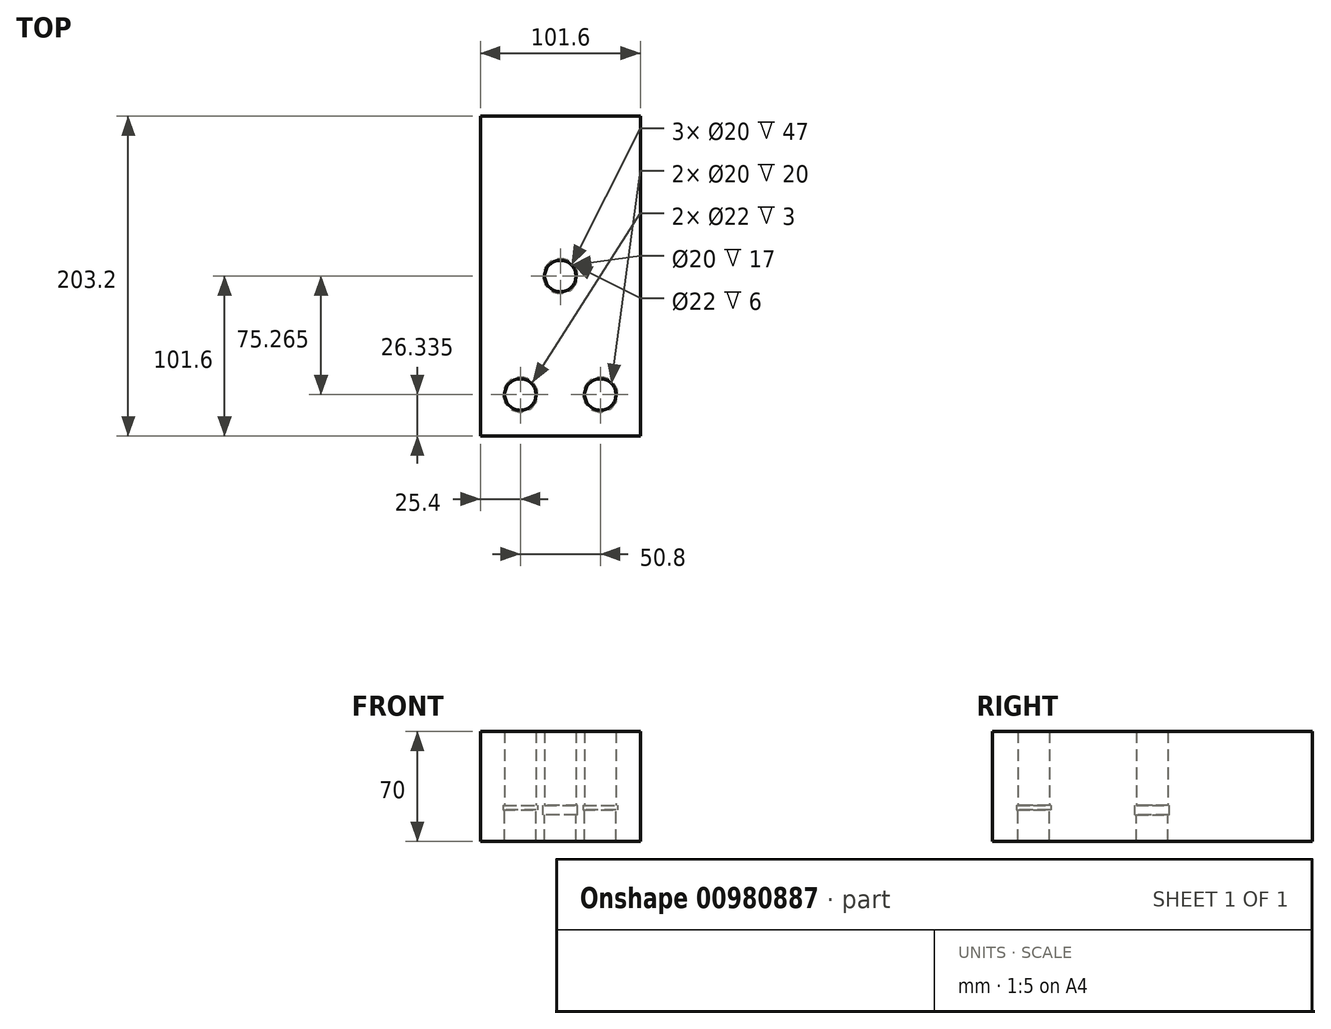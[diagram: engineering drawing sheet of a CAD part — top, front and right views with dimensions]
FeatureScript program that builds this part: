
annotation { "Feature Type Name" : "Feature", "Feature Type Description" : "" }
export const myFeature = defineFeature(function(context is Context, id is Id, definition is map)
    precondition{}
    {
        {
            var Q0;
            Q0=qCreatedBy(makeId("Top.planeOp"),FACE);
            var sketch = newSketch(context, id + "F0", { "sketchPlane" : qUnion([Q0])});
            skLineSegment(sketch, "E0.bottom", {"start": v(-50.8, -101.6) * mm, "end": v(50.8, -101.6) * mm});
            skLineSegment(sketch, "E0.top", {"start": v(-50.8, 101.6) * mm, "end": v(50.8, 101.6) * mm});
            skLineSegment(sketch, "E0.left", {"start": v(-50.8, -101.6) * mm, "end": v(-50.8, 101.6) * mm});
            skLineSegment(sketch, "E0.right", {"start": v(50.8, -101.6) * mm, "end": v(50.8, 101.6) * mm});
            skPoint(sketch, "E0.middle", {"position": v(0, 0) * mm});
            skPoint(sketch, "E1", {"position": v(-25.4, -75.26) * mm});
            skPoint(sketch, "E2", {"position": v(25.4, -75.26) * mm});
            skSolve(sketch);
        }
        {
            var Q0;
            Q0 = qSketchRegion(id + "F0", true);
            extrude(context, id + "F1", {"entities" : qUnion([Q0]), "oppositeDirection" : true, "depth" : 20 * mm, "offsetDistance" : 25.4 * mm});
        }
        {
            var Q0;
            Q0=sQuery(id+"F0.wireOp",VERTEX,"E0.middle");
            var Q1;
            Q1=makeQuery(id+"F1.opExtrude","SWEPT_BODY",BODY,{"disambiguationData":[OSD([sQuery(id+"F0.wireOp",EDGE,"E0.bottom"),sQuery(id+"F0.wireOp",EDGE,"E0.top"),sQuery(id+"F0.wireOp",EDGE,"E0.left"),sQuery(id+"F0.wireOp",EDGE,"E0.right")])]});
            hole(context, id + "F2", {"style" : HoleStyle.C_BORE, "endStyle" : HoleEndStyle.THROUGH, "holeDiameter" : 20 * mm, "cBoreDiameter" : 22 * mm, "cBoreDepth" : 3 * mm, "majorDiameter" : 6.35 * mm, "isTappedThrough" : true, "tappedDepth" : 12.7 * mm, "tapClearance" : 3, "startFromSketch" : true, "locations" : qUnion([Q0]), "scope" : qUnion([Q1])});
        }
        {
            var Q0;
            Q0=sQuery(id+"F0.wireOp",VERTEX,"E1");
            var Q1;
            Q1=makeQuery(id+"F1.opExtrude","SWEPT_BODY",BODY,{"disambiguationData":[OSD([sQuery(id+"F0.wireOp",EDGE,"E0.bottom"),sQuery(id+"F0.wireOp",EDGE,"E0.top"),sQuery(id+"F0.wireOp",EDGE,"E0.left"),sQuery(id+"F0.wireOp",EDGE,"E0.right")])]});
            hole(context, id + "F3", {"style" : HoleStyle.SIMPLE, "endStyle" : HoleEndStyle.THROUGH, "holeDiameter" : 20 * mm, "majorDiameter" : 6.35 * mm, "isTappedThrough" : true, "tappedDepth" : 12.7 * mm, "tapClearance" : 3, "startFromSketch" : true, "locations" : qUnion([Q0]), "scope" : qUnion([Q1])});
        }
        {
            var Q0;
            Q0=sQuery(id+"F0.wireOp",VERTEX,"E2");
            var Q1;
            Q1=makeQuery(id+"F1.opExtrude","SWEPT_BODY",BODY,{"disambiguationData":[OSD([sQuery(id+"F0.wireOp",EDGE,"E0.bottom"),sQuery(id+"F0.wireOp",EDGE,"E0.top"),sQuery(id+"F0.wireOp",EDGE,"E0.left"),sQuery(id+"F0.wireOp",EDGE,"E0.right")])]});
            hole(context, id + "F4", {"style" : HoleStyle.SIMPLE, "endStyle" : HoleEndStyle.THROUGH, "holeDiameter" : 20 * mm, "majorDiameter" : 6.35 * mm, "isTappedThrough" : true, "tappedDepth" : 12.7 * mm, "tapClearance" : 3, "startFromSketch" : true, "locations" : qUnion([Q0]), "scope" : qUnion([Q1])});
        }
        {
            var Q0;
            Q0=makeQuery(id+"F0.imprint","IMPRINT",FACE,{"disambiguationData":[TD([[makeQuery(id+"F0.imprint","IMPRINT",EDGE,{"derivedFrom":sQuery(id+"F0.wireOp",EDGE,"E0.bottom")}),1.0]])]});
            var sketch = newSketch(context, id + "F5", { "sketchPlane" : qUnion([Q0])});
            skCircle(sketch, "E3", {"center": v(0, 76.88) * mm, "radius": 5.96 * mm});
            skSolve(sketch);
        }
        {
            var Q0;
            Q0 = qSketchRegion(id + "F5", true);
            var Q1;
            Q1=makeQuery(id+"F0.imprint","IMPRINT",FACE,{"disambiguationData":[TD([[makeQuery(id+"F0.imprint","IMPRINT",EDGE,{"derivedFrom":sQuery(id+"F0.wireOp",EDGE,"E0.bottom")}),1.0]])]});
            extrude(context, id + "F6", {"entities" : qUnion([Q0, Q1]), "operationType" : NewBodyOperationType.ADD, "depth" : 50 * mm, "offsetDistance" : 25.4 * mm});
        }
        {
            var Q0;
            Q0=sQuery(id+"F0.wireOp",VERTEX,"E0.middle");
            var Q1;
            Q1=makeQuery(id+"F1.opExtrude","SWEPT_BODY",BODY,{"disambiguationData":[OSD([sQuery(id+"F0.wireOp",EDGE,"E0.bottom"),sQuery(id+"F0.wireOp",EDGE,"E0.top"),sQuery(id+"F0.wireOp",EDGE,"E0.left"),sQuery(id+"F0.wireOp",EDGE,"E0.right")])]});
            hole(context, id + "F7", {"style" : HoleStyle.C_BORE, "endStyle" : HoleEndStyle.THROUGH, "oppositeDirection" : true, "holeDiameter" : 20 * mm, "cBoreDiameter" : 22 * mm, "cBoreDepth" : 3 * mm, "majorDiameter" : 6.35 * mm, "isTappedThrough" : true, "tappedDepth" : 12.7 * mm, "tapClearance" : 3, "startFromSketch" : true, "locations" : qUnion([Q0]), "scope" : qUnion([Q1])});
        }
        {
            var Q0;
            Q0=sQuery(id+"F0.wireOp",VERTEX,"E2");
            var Q1;
            Q1=makeQuery(id+"F1.opExtrude","SWEPT_BODY",BODY,{"disambiguationData":[OSD([sQuery(id+"F0.wireOp",EDGE,"E0.bottom"),sQuery(id+"F0.wireOp",EDGE,"E0.top"),sQuery(id+"F0.wireOp",EDGE,"E0.left"),sQuery(id+"F0.wireOp",EDGE,"E0.right")])]});
            hole(context, id + "F8", {"style" : HoleStyle.C_BORE, "endStyle" : HoleEndStyle.THROUGH, "oppositeDirection" : true, "holeDiameter" : 20 * mm, "cBoreDiameter" : 22 * mm, "cBoreDepth" : 3 * mm, "majorDiameter" : 6.35 * mm, "isTappedThrough" : true, "tappedDepth" : 12.7 * mm, "tapClearance" : 3, "startFromSketch" : true, "locations" : qUnion([Q0]), "scope" : qUnion([Q1])});
        }
        {
            var Q0;
            Q0=sQuery(id+"F0.wireOp",VERTEX,"E1");
            var Q1;
            Q1=makeQuery(id+"F1.opExtrude","SWEPT_BODY",BODY,{"disambiguationData":[OSD([sQuery(id+"F0.wireOp",EDGE,"E0.bottom"),sQuery(id+"F0.wireOp",EDGE,"E0.top"),sQuery(id+"F0.wireOp",EDGE,"E0.left"),sQuery(id+"F0.wireOp",EDGE,"E0.right")])]});
            hole(context, id + "F9", {"style" : HoleStyle.C_BORE, "endStyle" : HoleEndStyle.THROUGH, "oppositeDirection" : true, "holeDiameter" : 20 * mm, "cBoreDiameter" : 22 * mm, "cBoreDepth" : 3 * mm, "majorDiameter" : 6.35 * mm, "isTappedThrough" : true, "tappedDepth" : 12.7 * mm, "tapClearance" : 3, "startFromSketch" : true, "locations" : qUnion([Q0]), "scope" : qUnion([Q1])});
        }
    });
